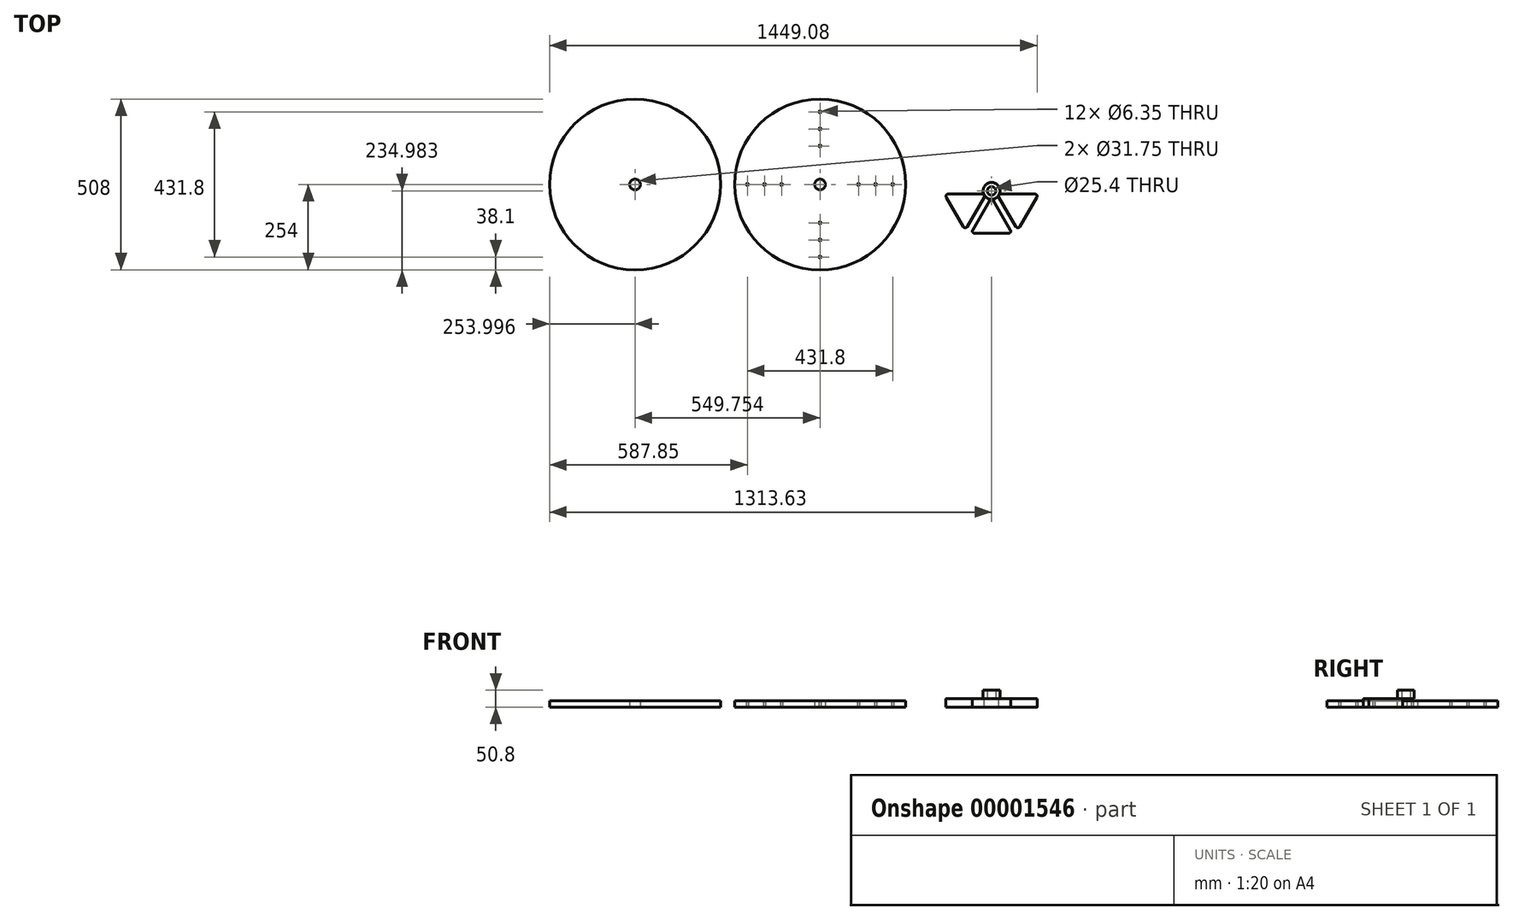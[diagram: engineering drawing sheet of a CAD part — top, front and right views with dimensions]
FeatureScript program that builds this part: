
annotation { "Feature Type Name" : "Feature", "Feature Type Description" : "" }
export const myFeature = defineFeature(function(context is Context, id is Id, definition is map)
    precondition{}
    {
        {
            var Q0;
            Q0=qCreatedBy(makeId("Top.planeOp"),FACE);
            var sketch = newSketch(context, id + "F0", { "sketchPlane" : qUnion([Q0])});
            skCircle(sketch, "E0", {"center": v(0, 0) * mm, "radius": 254 * mm});
            skCircle(sketch, "E1", {"center": v(0, 0) * mm, "radius": 15.88 * mm});
            skCircle(sketch, "E2", {"center": v(-114.3, 0) * mm, "radius": 3.18 * mm});
            skCircle(sketch, "E3", {"center": v(0, 114.3) * mm, "radius": 3.18 * mm});
            skCircle(sketch, "E4", {"center": v(114.3, 0) * mm, "radius": 3.18 * mm});
            skCircle(sketch, "E5", {"center": v(0, -114.3) * mm, "radius": 3.18 * mm});
            skCircle(sketch, "E6", {"center": v(-165.1, 0) * mm, "radius": 3.18 * mm});
            skCircle(sketch, "E7", {"center": v(-215.9, 0) * mm, "radius": 3.18 * mm});
            skCircle(sketch, "E8", {"center": v(0, -165.1) * mm, "radius": 3.18 * mm});
            skCircle(sketch, "E9", {"center": v(0, -215.9) * mm, "radius": 3.18 * mm});
            skCircle(sketch, "E10", {"center": v(165.1, 0) * mm, "radius": 3.18 * mm});
            skCircle(sketch, "E11", {"center": v(215.9, 0) * mm, "radius": 3.18 * mm});
            skCircle(sketch, "E12", {"center": v(0, 165.1) * mm, "radius": 3.18 * mm});
            skCircle(sketch, "E13", {"center": v(0, 215.9) * mm, "radius": 3.18 * mm});
            skSolve(sketch);
        }
        {
            var Q0;
            Q0=makeQuery(id+"F0.imprint","IMPRINT",FACE,{"disambiguationData":[TD([[makeQuery(id+"F0.imprint","IMPRINT",EDGE,{"derivedFrom":sQuery(id+"F0.wireOp",EDGE,"E0")}),1.0]])]});
            extrude(context, id + "F1", {"entities" : qUnion([Q0]), "depth" : 19.05 * mm});
        }
        {
            var Q0;
            Q0=qCreatedBy(makeId("Top.planeOp"),FACE);
            var sketch = newSketch(context, id + "F2", { "sketchPlane" : qUnion([Q0])});
            skCircle(sketch, "E14", {"center": v(-549.75, 0) * mm, "radius": 254 * mm});
            skCircle(sketch, "E15", {"center": v(-549.75, 0) * mm, "radius": 15.88 * mm});
            skSolve(sketch);
        }
        {
            var Q0;
            Q0=qCreatedBy(makeId("Top.planeOp"),FACE);
            var sketch = newSketch(context, id + "F3", { "sketchPlane" : qUnion([Q0])});
            skCircle(sketch, "E16", {"center": v(509.88, -19.02) * mm, "radius": 152.4 * mm});
            skCircle(sketch, "E17", {"center": v(509.88, -19.02) * mm, "radius": 12.7 * mm});
            skCircle(sketch, "E18", {"center": v(509.88, -19.02) * mm, "radius": 31.75 * mm});
            skCircle(sketch, "E19", {"center": v(509.88, -19.02) * mm, "radius": 133.35 * mm});
            skSolve(sketch);
        }
        {
            var Q0;
            Q0=makeQuery(id+"F3.imprint","IMPRINT",FACE,{"disambiguationData":[TD([[makeQuery(id+"F3.imprint","IMPRINT",EDGE,{"derivedFrom":sQuery(id+"F3.wireOp",EDGE,"E16")}),1.0]])]});
            var Q1;
            Q1=makeQuery(id+"F3.imprint","IMPRINT",FACE,{"disambiguationData":[TD([[makeQuery(id+"F3.imprint","IMPRINT",EDGE,{"derivedFrom":sQuery(id+"F3.wireOp",EDGE,"E17")}),-1.0]])]});
            var Q2;
            Q2=makeQuery(id+"F3.imprint","IMPRINT",FACE,{"disambiguationData":[TD([[makeQuery(id+"F3.imprint","IMPRINT",EDGE,{"derivedFrom":sQuery(id+"F3.wireOp",EDGE,"E18")}),-1.0]])]});
            extrude(context, id + "F4", {"entities" : qUnion([Q0, Q1, Q2]), "depth" : 25.4 * mm});
        }
        {
            var Q0;
            Q0=makeQuery(id+"F4.opExtrude","CAP_FACE",FACE,{"disambiguationData":[OSD([sQuery(id+"F3.wireOp",EDGE,"E16"),sQuery(id+"F3.wireOp",EDGE,"E17")])],"isStart":false});
            var sketch = newSketch(context, id + "F5", { "sketchPlane" : qUnion([Q0])});
            skSolve(sketch);
        }
        {
            var Q0;
            Q0=makeQuery(id+"F5.imprint","IMPRINT",FACE,{"disambiguationData":[TD([[makeQuery(id+"F5.imprint","IMPRINT",EDGE,{"derivedFrom":makeQuery(id+"F4.opExtrude","CAP_EDGE",EDGE,{"disambiguationData":[OSD([sQuery(id+"F3.wireOp",EDGE,"E16")])],"isStart":false})}),1.0]])]});
            var sketch = newSketch(context, id + "F6", { "sketchPlane" : qUnion([Q0])});
            skLineSegment(sketch, "E20.0", {"start": v(459.08, 107.07) * mm, "end": v(560.68, 107.07) * mm});
            skLineSegment(sketch, "E20.1", {"start": v(566.18, 97.55) * mm, "end": v(515.38, 9.56) * mm});
            skLineSegment(sketch, "E20.2", {"start": v(504.38, 9.56) * mm, "end": v(453.58, 97.55) * mm});
            skPoint(sketch, "E20.0.midPoint", {"position": v(509.88, 107.07) * mm});
            skPoint(sketch, "E21.visualSharp", {"position": v(448.08, 107.07) * mm});
            skArc(sketch, "E21.filletArc", {"start": v(459.08, 107.07) * mm, "mid": v(453.58, 103.9) * mm, "end": v(453.58, 97.55) * mm});
            skPoint(sketch, "E22.visualSharp", {"position": v(509.88, 0.03) * mm});
            skArc(sketch, "E22.filletArc", {"start": v(504.38, 9.56) * mm, "mid": v(509.88, 6.38) * mm, "end": v(515.38, 9.56) * mm});
            skPoint(sketch, "E23.visualSharp", {"position": v(571.68, 107.07) * mm});
            skArc(sketch, "E23.filletArc", {"start": v(566.18, 97.55) * mm, "mid": v(566.18, 103.9) * mm, "end": v(560.68, 107.07) * mm});
            skLineSegment(sketch, "E24.0", {"start": v(437.08, 88.02) * mm, "end": v(487.88, 0.03) * mm});
            skLineSegment(sketch, "E24.1", {"start": v(482.39, -9.5) * mm, "end": v(380.79, -9.5) * mm});
            skLineSegment(sketch, "E24.2", {"start": v(375.29, 0.03) * mm, "end": v(426.09, 88.02) * mm});
            skPoint(sketch, "E24.0.midPoint", {"position": v(462.48, 44.03) * mm});
            skPoint(sketch, "E25.visualSharp", {"position": v(369.79, -9.5) * mm});
            skArc(sketch, "E25.filletArc", {"start": v(375.29, 0.03) * mm, "mid": v(375.29, -6.32) * mm, "end": v(380.79, -9.5) * mm});
            skPoint(sketch, "E26.visualSharp", {"position": v(431.59, 97.55) * mm});
            skArc(sketch, "E26.filletArc", {"start": v(437.08, 88.02) * mm, "mid": v(431.59, 91.2) * mm, "end": v(426.09, 88.02) * mm});
            skPoint(sketch, "E27.visualSharp", {"position": v(493.38, -9.5) * mm});
            skArc(sketch, "E27.filletArc", {"start": v(482.39, -9.5) * mm, "mid": v(487.88, -6.32) * mm, "end": v(487.88, 0.03) * mm});
            skLineSegment(sketch, "E28.0", {"start": v(531.88, 0.03) * mm, "end": v(582.68, 88.02) * mm});
            skLineSegment(sketch, "E28.1", {"start": v(593.68, 88.02) * mm, "end": v(644.48, 0.03) * mm});
            skLineSegment(sketch, "E28.2", {"start": v(638.98, -9.5) * mm, "end": v(537.38, -9.5) * mm});
            skPoint(sketch, "E28.0.midPoint", {"position": v(557.28, 44.03) * mm});
            skPoint(sketch, "E29.visualSharp", {"position": v(588.18, 97.55) * mm});
            skArc(sketch, "E29.filletArc", {"start": v(593.68, 88.02) * mm, "mid": v(588.18, 91.2) * mm, "end": v(582.68, 88.02) * mm});
            skPoint(sketch, "E30.visualSharp", {"position": v(649.98, -9.5) * mm});
            skArc(sketch, "E30.filletArc", {"start": v(638.98, -9.5) * mm, "mid": v(644.48, -6.32) * mm, "end": v(644.48, 0.03) * mm});
            skPoint(sketch, "E31.visualSharp", {"position": v(526.38, -9.5) * mm});
            skArc(sketch, "E31.filletArc", {"start": v(531.88, 0.03) * mm, "mid": v(531.88, -6.32) * mm, "end": v(537.38, -9.5) * mm});
            skArc(sketch, "E32.0.MirrorCS", {"start": v(566.18, -135.58) * mm, "mid": v(566.18, -141.93) * mm, "end": v(560.68, -145.1) * mm});
            skArc(sketch, "E32.1.MirrorCS", {"start": v(638.98, -28.54) * mm, "mid": v(644.48, -31.72) * mm, "end": v(644.48, -38.07) * mm});
            skPoint(sketch, "E32.2.MirrorP", {"position": v(462.48, -82.06) * mm});
            skArc(sketch, "E32.3.MirrorCS", {"start": v(531.88, -38.07) * mm, "mid": v(531.88, -31.72) * mm, "end": v(537.38, -28.54) * mm});
            skPoint(sketch, "E32.4.MirrorP", {"position": v(557.28, -82.06) * mm});
            skPoint(sketch, "E32.5.MirrorP", {"position": v(649.98, -28.54) * mm});
            skPoint(sketch, "E32.6.MirrorP", {"position": v(448.08, -145.1) * mm});
            skPoint(sketch, "E32.7.MirrorP", {"position": v(588.18, -135.58) * mm});
            skArc(sketch, "E32.8.MirrorCS", {"start": v(375.29, -38.07) * mm, "mid": v(375.29, -31.72) * mm, "end": v(380.79, -28.54) * mm});
            skLineSegment(sketch, "E32.9.MirrorCS", {"start": v(437.08, -126.06) * mm, "end": v(487.88, -38.07) * mm});
            skPoint(sketch, "E32.10.MirrorP", {"position": v(431.59, -135.58) * mm});
            skArc(sketch, "E32.11.MirrorCS", {"start": v(437.08, -126.06) * mm, "mid": v(431.59, -129.23) * mm, "end": v(426.09, -126.06) * mm});
            skArc(sketch, "E32.12.MirrorCS", {"start": v(482.39, -28.54) * mm, "mid": v(487.88, -31.72) * mm, "end": v(487.88, -38.07) * mm});
            skPoint(sketch, "E32.13.MirrorP", {"position": v(493.38, -28.54) * mm});
            skArc(sketch, "E32.14.MirrorCS", {"start": v(593.68, -126.06) * mm, "mid": v(588.18, -129.23) * mm, "end": v(582.68, -126.06) * mm});
            skLineSegment(sketch, "E32.15.MirrorCS", {"start": v(638.98, -28.54) * mm, "end": v(537.38, -28.54) * mm});
            skPoint(sketch, "E32.16.MirrorP", {"position": v(526.38, -28.54) * mm});
            skLineSegment(sketch, "E32.17.MirrorCS", {"start": v(482.39, -28.54) * mm, "end": v(380.79, -28.54) * mm});
            skLineSegment(sketch, "E32.18.MirrorCS", {"start": v(531.88, -38.07) * mm, "end": v(582.68, -126.06) * mm});
            skLineSegment(sketch, "E32.19.MirrorCS", {"start": v(375.29, -38.07) * mm, "end": v(426.09, -126.06) * mm});
            skLineSegment(sketch, "E32.20.MirrorCS", {"start": v(459.08, -145.1) * mm, "end": v(560.68, -145.1) * mm});
            skLineSegment(sketch, "E32.21.MirrorCS", {"start": v(593.68, -126.06) * mm, "end": v(644.48, -38.07) * mm});
            skLineSegment(sketch, "E32.22.MirrorCS", {"start": v(566.18, -135.58) * mm, "end": v(515.38, -47.6) * mm});
            skPoint(sketch, "E32.23.MirrorP", {"position": v(369.79, -28.54) * mm});
            skPoint(sketch, "E32.24.MirrorP", {"position": v(509.88, -145.1) * mm});
            skArc(sketch, "E32.25.MirrorCS", {"start": v(504.38, -47.6) * mm, "mid": v(509.88, -44.42) * mm, "end": v(515.38, -47.6) * mm});
            skPoint(sketch, "E32.26.MirrorP", {"position": v(509.88, -38.07) * mm});
            skArc(sketch, "E32.27.MirrorCS", {"start": v(459.08, -145.1) * mm, "mid": v(453.58, -141.93) * mm, "end": v(453.58, -135.58) * mm});
            skLineSegment(sketch, "E32.28.MirrorCS", {"start": v(504.38, -47.6) * mm, "end": v(453.58, -135.58) * mm});
            skPoint(sketch, "E32.29.MirrorP", {"position": v(571.68, -145.1) * mm});
            skSolve(sketch);
        }
        {
            var Q0;
            {Q0=qUnion([makeQuery(id+"F6.imprint","IMPRINT",FACE,{"disambiguationData":[TD([[makeQuery(id+"F6.imprint","IMPRINT",EDGE,{"derivedFrom":sQuery(id+"F6.wireOp",EDGE,"E20.0")}),-1.0]])]}),makeQuery(id+"F6.imprint","IMPRINT",FACE,{"disambiguationData":[TD([[makeQuery(id+"F6.imprint","IMPRINT",EDGE,{"derivedFrom":sQuery(id+"F6.wireOp",EDGE,"E24.0")}),-1.0]])]}),makeQuery(id+"F6.imprint","IMPRINT",FACE,{"disambiguationData":[TD([[makeQuery(id+"F6.imprint","IMPRINT",EDGE,{"derivedFrom":sQuery(id+"F6.wireOp",EDGE,"E28.0")}),-1.0]])]}),makeQuery(id+"F6.imprint","IMPRINT",FACE,{"disambiguationData":[TD([[makeQuery(id+"F6.imprint","IMPRINT",EDGE,{"derivedFrom":sQuery(id+"F6.wireOp",EDGE,"E32.0.MirrorCS")}),-1.0]])]}),makeQuery(id+"F6.imprint","IMPRINT",FACE,{"disambiguationData":[TD([[makeQuery(id+"F6.imprint","IMPRINT",EDGE,{"derivedFrom":sQuery(id+"F6.wireOp",EDGE,"E32.1.MirrorCS")}),-1.0]])]}),makeQuery(id+"F6.imprint","IMPRINT",FACE,{"disambiguationData":[TD([[makeQuery(id+"F6.imprint","IMPRINT",EDGE,{"derivedFrom":sQuery(id+"F6.wireOp",EDGE,"E32.8.MirrorCS")}),-1.0]])]})]);}
            extrude(context, id + "F7", {"entities" : qUnion([Q0]), "operationType" : NewBodyOperationType.REMOVE, "oppositeDirection" : true, "depth" : 25.4 * mm});
        }
        {
            var Q0;
            Q0=makeQuery(id+"F2.imprint","IMPRINT",FACE,{"disambiguationData":[TD([[makeQuery(id+"F2.imprint","IMPRINT",EDGE,{"derivedFrom":sQuery(id+"F2.wireOp",EDGE,"E14")}),1.0]])]});
            extrude(context, id + "F8", {"entities" : qUnion([Q0]), "depth" : 19.05 * mm});
        }
        {
            var Q0;
            Q0=makeQuery(id+"F5.imprint","IMPRINT",FACE,{"disambiguationData":[TD([[makeQuery(id+"F5.imprint","IMPRINT",EDGE,{"derivedFrom":makeQuery(id+"F4.opExtrude","CAP_EDGE",EDGE,{"disambiguationData":[OSD([sQuery(id+"F3.wireOp",EDGE,"E16")])],"isStart":false})}),1.0]])]});
            var sketch = newSketch(context, id + "F9", { "sketchPlane" : qUnion([Q0])});
            skCircle(sketch, "E33.0", {"center": v(509.88, -19.02) * mm, "radius": 12.7 * mm});
            skCircle(sketch, "E34", {"center": v(509.88, -19.02) * mm, "radius": 25.09 * mm});
            skCircle(sketch, "E35", {"center": v(509.88, -19.02) * mm, "radius": 12.61 * mm});
            skSolve(sketch);
        }
        {
            var Q0;
            Q0=makeQuery(id+"F9.imprint","IMPRINT",FACE,{"disambiguationData":[TD([[makeQuery(id+"F9.imprint","IMPRINT",EDGE,{"derivedFrom":sQuery(id+"F9.wireOp",EDGE,"E33.0")}),-1.0]])]});
            var Q1;
            Q1=sQuery(id+"F9.wireOp",EDGE,"E34");
            extrude(context, id + "F10", {"entities" : qUnion([Q0]), "operationType" : NewBodyOperationType.ADD, "surfaceEntities" : qUnion([Q1]), "depth" : 25.4 * mm});
        }
    });
